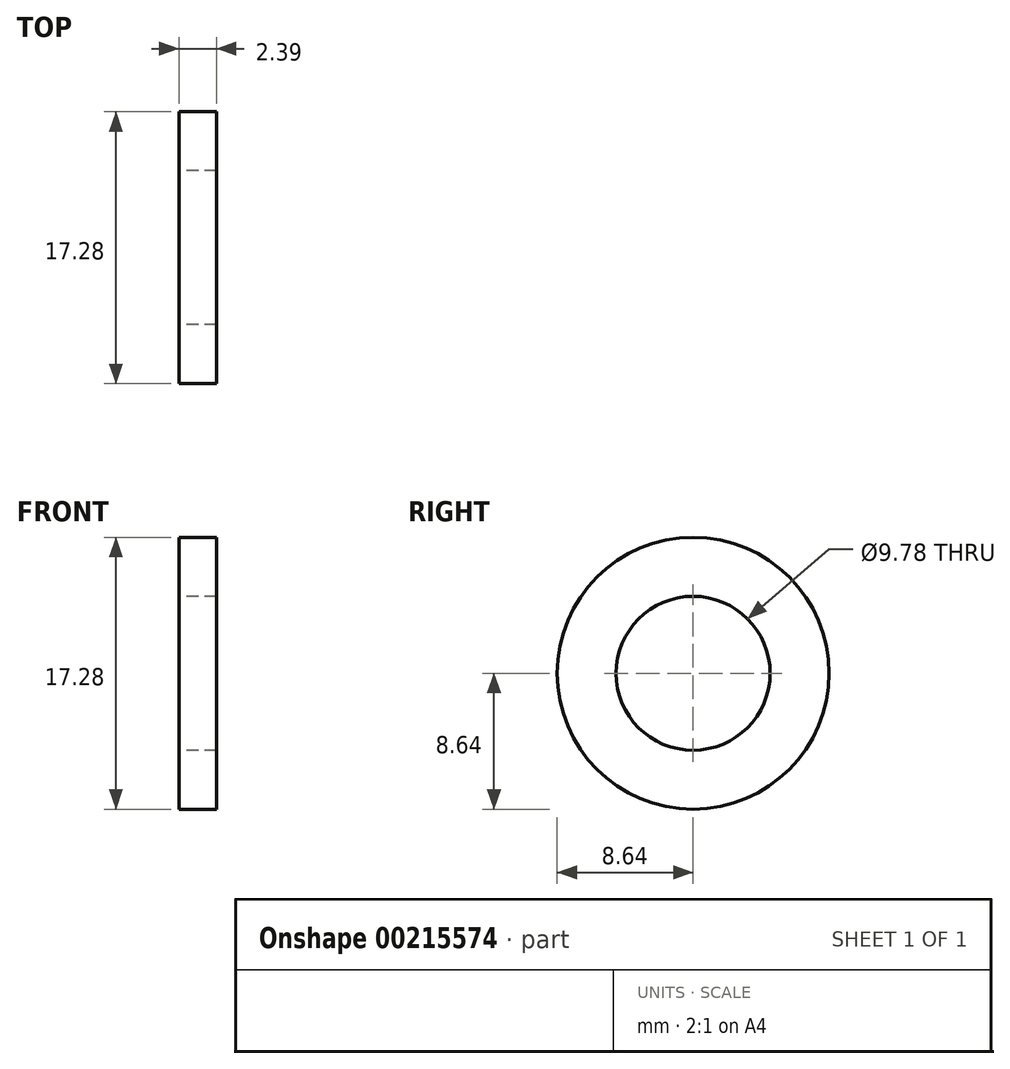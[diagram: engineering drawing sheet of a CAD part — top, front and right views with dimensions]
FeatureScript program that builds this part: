
annotation { "Feature Type Name" : "Feature", "Feature Type Description" : "" }
export const myFeature = defineFeature(function(context is Context, id is Id, definition is map)
    precondition{}
    {
        {
            var Q0;
            Q0=qCreatedBy(makeId("Right.planeOp"),FACE);
            var sketch = newSketch(context, id + "F0", { "sketchPlane" : qUnion([Q0])});
            skCircle(sketch, "E0", {"center": v(0, 0) * mm, "radius": 8.64 * mm});
            skCircle(sketch, "E1", {"center": v(0, 0) * mm, "radius": 4.89 * mm});
            skSolve(sketch);
        }
        {
            var Q0;
            Q0=makeQuery(id+"F0.imprint","IMPRINT",FACE,{"disambiguationData":[TD([[makeQuery(id+"F0.imprint","IMPRINT",EDGE,{"derivedFrom":sQuery(id+"F0.wireOp",EDGE,"E0")}),1.0]])]});
            extrude(context, id + "F1", {"entities" : qUnion([Q0]), "depth" : 2.4 * mm});
        }
    });
